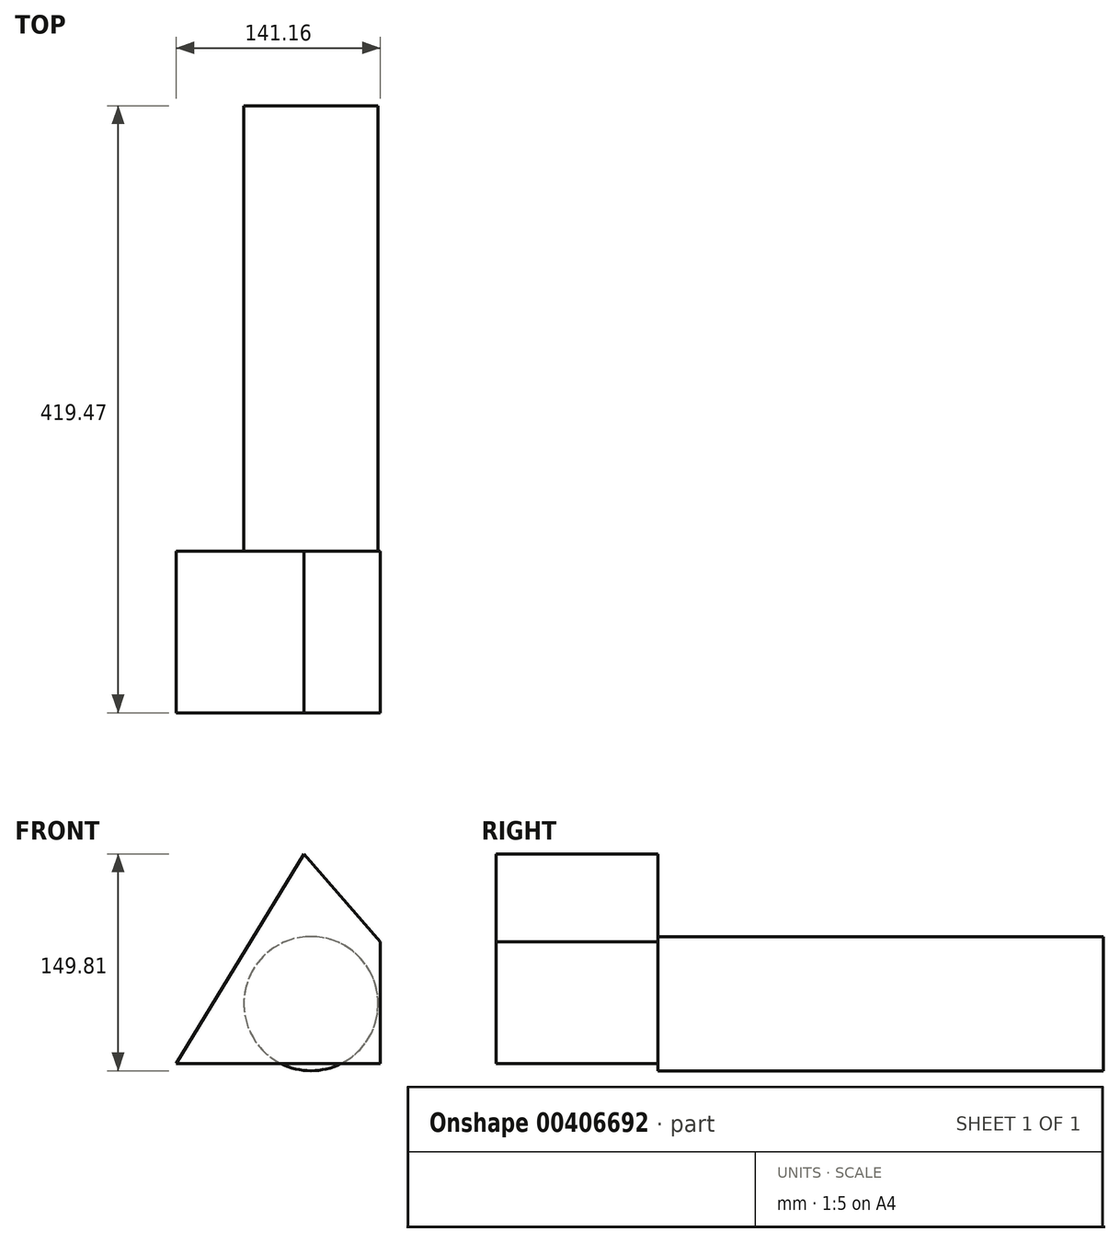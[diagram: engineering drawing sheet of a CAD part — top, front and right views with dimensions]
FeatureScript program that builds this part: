
annotation { "Feature Type Name" : "Feature", "Feature Type Description" : "" }
export const myFeature = defineFeature(function(context is Context, id is Id, definition is map)
    precondition{}
    {
        {
            var Q0;
            Q0=qCreatedBy(makeId("Front.planeOp"),FACE);
            var sketch = newSketch(context, id + "F0", { "sketchPlane" : qUnion([Q0])});
            skLineSegment(sketch, "E0", {"start": v(141.16, 0) * mm, "end": v(141.16, 0) * mm});
            skLineSegment(sketch, "E1", {"start": v(141.16, 0) * mm, "end": v(0, 0) * mm});
            skLineSegment(sketch, "E2", {"start": v(0, 0) * mm, "end": v(88.5, 144.96) * mm});
            skLineSegment(sketch, "E3", {"start": v(88.5, 144.96) * mm, "end": v(88.5, 144.96) * mm});
            skLineSegment(sketch, "E4", {"start": v(141.16, 84.29) * mm, "end": v(88.5, 144.96) * mm});
            skLineSegment(sketch, "E5", {"start": v(141.16, -54.94) * mm, "end": v(141.16, 84.29) * mm});
            skSolve(sketch);
        }
        {
            var Q0;
            Q0 = qSketchRegion(id + "F0", true);
            extrude(context, id + "F1", {"entities" : qUnion([Q0]), "depth" : 111.65 * mm});
        }
        {
            var Q0;
            Q0=makeQuery(id+"F1.opExtrude","CAP_FACE",FACE,{"disambiguationData":[OSD([sQuery(id+"F0.wireOp",EDGE,"E1"),sQuery(id+"F0.wireOp",EDGE,"E2"),sQuery(id+"F0.wireOp",EDGE,"E4"),sQuery(id+"F0.wireOp",EDGE,"E5")])],"isStart":true});
            var sketch = newSketch(context, id + "F2", { "sketchPlane" : qUnion([Q0])});
            skCircle(sketch, "E6", {"center": v(-93.25, 41.5) * mm, "radius": 46.36 * mm});
            skSolve(sketch);
        }
        {
            var Q0;
            Q0 = qSketchRegion(id + "F2", true);
            extrude(context, id + "F3", {"entities" : qUnion([Q0]), "operationType" : NewBodyOperationType.ADD, "depth" : 307.82 * mm});
        }
    });
